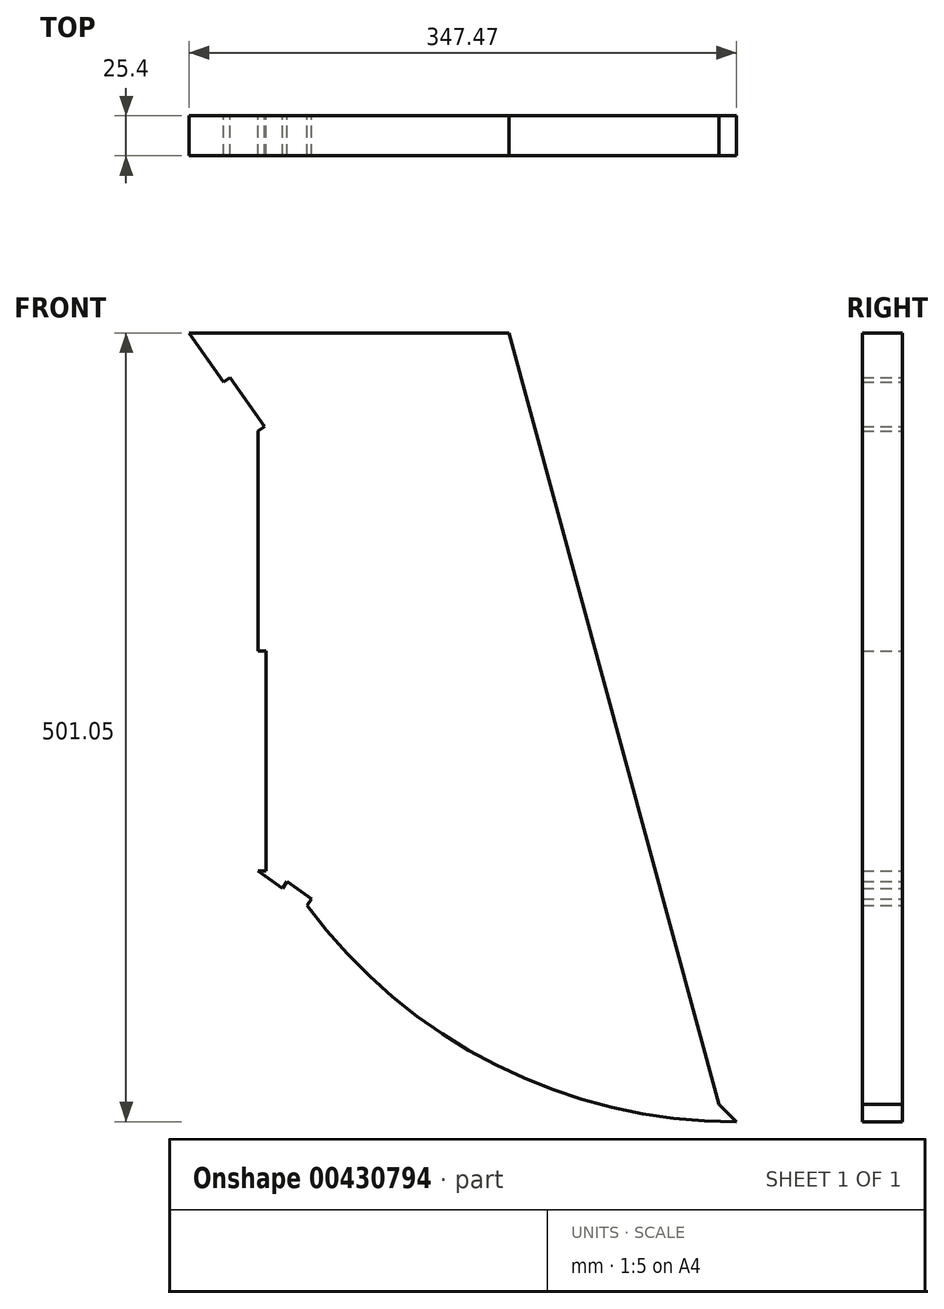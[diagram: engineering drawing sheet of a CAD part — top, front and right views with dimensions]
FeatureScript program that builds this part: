
annotation { "Feature Type Name" : "Feature", "Feature Type Description" : "" }
export const myFeature = defineFeature(function(context is Context, id is Id, definition is map)
    precondition{}
    {
        {
            var Q0;
            Q0=qCreatedBy(makeId("Front.planeOp"),FACE);
            var sketch = newSketch(context, id + "F0", { "sketchPlane" : qUnion([Q0])});
            skLineSegment(sketch, "E0", {"start": v(0, 0) * mm, "end": v(203.2, 0) * mm});
            skLineSegment(sketch, "E1", {"start": v(203.2, 0) * mm, "end": v(336.54, -490.19) * mm});
            skArc(sketch, "E2.0", {"start": v(74.92, -363.67) * mm, "mid": v(194.73, -465.03) * mm, "end": v(347.47, -501.04) * mm});
            skLineSegment(sketch, "E2.1", {"start": v(43.7, -341.82) * mm, "end": v(59.31, -352.75) * mm});
            skLineSegment(sketch, "E2.2", {"start": v(43.7, -62.42) * mm, "end": v(43.7, -202.12) * mm});
            skLineSegment(sketch, "E2.3", {"start": v(0, 0) * mm, "end": v(21.85, -31.2) * mm});
            skLineSegment(sketch, "E3", {"start": v(347.47, -501.04) * mm, "end": v(336.54, -490.19) * mm});
            skLineSegment(sketch, "E4", {"start": v(347.47, -501.04) * mm, "end": v(737.25, -499.57) * mm, "construction": true});
            skLineSegment(sketch, "E5.bottom", {"start": v(43.7, -341.82) * mm, "end": v(48.79, -341.82) * mm});
            skLineSegment(sketch, "E5.top", {"start": v(43.7, -202.12) * mm, "end": v(48.79, -202.12) * mm});
            skLineSegment(sketch, "E5.right", {"start": v(48.79, -341.82) * mm, "end": v(48.79, -202.12) * mm});
            skLineSegment(sketch, "E6", {"start": v(43.7, -62.42) * mm, "end": v(47.87, -59.5) * mm});
            skLineSegment(sketch, "E7", {"start": v(47.87, -59.5) * mm, "end": v(26.01, -28.3) * mm});
            skLineSegment(sketch, "E8", {"start": v(26.01, -28.3) * mm, "end": v(21.85, -31.2) * mm});
            skLineSegment(sketch, "E9", {"start": v(74.92, -363.67) * mm, "end": v(77.83, -359.51) * mm});
            skLineSegment(sketch, "E10", {"start": v(77.83, -359.51) * mm, "end": v(62.23, -348.58) * mm});
            skLineSegment(sketch, "E11", {"start": v(62.23, -348.58) * mm, "end": v(59.31, -352.75) * mm});
            skSolve(sketch);
        }
        {
            var Q0;
            Q0=makeQuery(id+"F0.imprint","IMPRINT",FACE,{"disambiguationData":[TD([[makeQuery(id+"F0.imprint","IMPRINT",EDGE,{"derivedFrom":sQuery(id+"F0.wireOp",EDGE,"E0")}),-1.0]])]});
            extrude(context, id + "F1", {"entities" : qUnion([Q0]), "depth" : 25.4 * mm});
        }
    });
